# Revit family: Bernhardt_Design-Tables-Multipurpose-LaPaz
name_source: partatom
category: Furniture
revit_build: Autodesk Revit 2016 (Build: 20150714_1515(x64)
units: mm (PartAtom-declared; Revit-internal decimal feet)

## family parameters
Always vertical = Yes
Cut with Voids When Loaded = No
OmniClass Number = 23.40.20.00
OmniClass Title = General Furniture and Specialties
Room Calculation Point = No
Shared = No
Work Plane-Based = No

## types (4) — shared parameters
Manufacturer = Bernhardt Design
Model = La Paz
URL = http://www.bernhardtdesign.com

## per-type parameters (varying)
| type | Catalog | Round 42 Top | Round 48 Top | SKU | Square Inner Radius | Square Radius | Square Top |
| La Paz - 42" Round | LPS-DBB | Yes | No | LPS-DBB | 17.336 " | 18 " | No |
| La Paz - 48" Round | LPS-DCC | No | Yes | LPS-DCC | 17.336 " | 18 " | No |
| La Paz - 36" Square | LPS-CAA | No | No | LPS-CAA | 17.336 " | 18 " | Yes |
| La Paz - 42" Square | LPS-CBB | No | No | LPS-CBB | 20.336 " | 21 " | Yes |

## geometry (parser evidence)
native form markers: Sweep x6
no freeform markers — native parametric forms only
